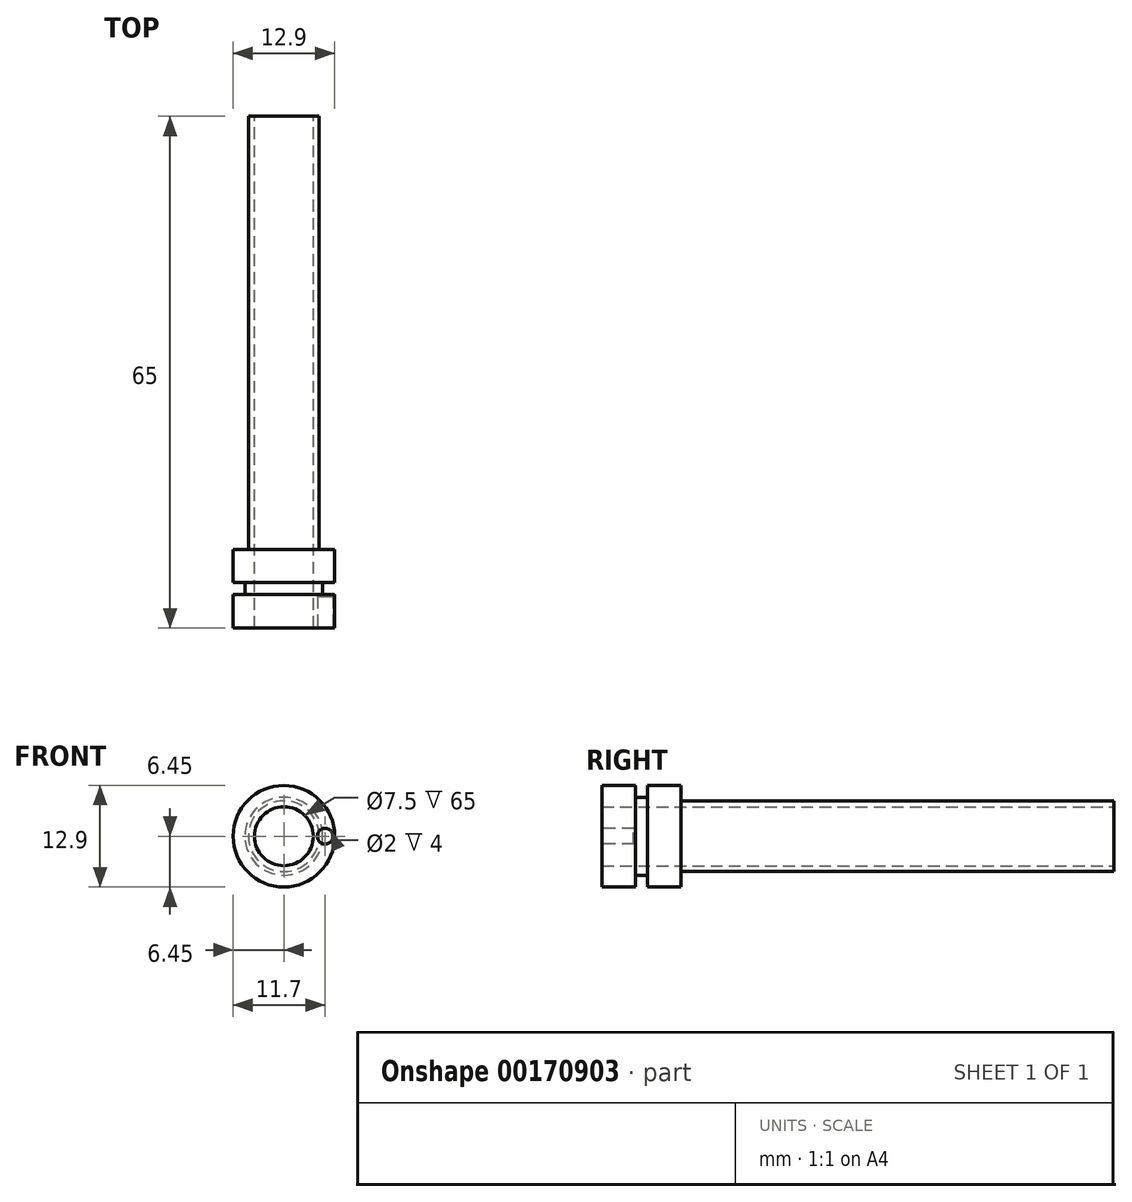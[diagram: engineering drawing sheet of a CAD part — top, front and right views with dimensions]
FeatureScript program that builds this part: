
annotation { "Feature Type Name" : "Feature", "Feature Type Description" : "" }
export const myFeature = defineFeature(function(context is Context, id is Id, definition is map)
    precondition{}
    {
        {
            var Q0;
            Q0=qCreatedBy(makeId("Right.planeOp"),FACE);
            var sketch = newSketch(context, id + "F0", { "sketchPlane" : qUnion([Q0])});
            skLineSegment(sketch, "E0", {"start": v(11.47, 0) * mm, "end": v(0, 0) * mm, "construction": true});
            skLineSegment(sketch, "E1", {"start": v(65, 3.75) * mm, "end": v(0, 3.75) * mm});
            skLineSegment(sketch, "E2", {"start": v(65, 0) * mm, "end": v(65, 3.75) * mm});
            skLineSegment(sketch, "E3", {"start": v(65, 0) * mm, "end": v(65, 0) * mm});
            skLineSegment(sketch, "E4", {"start": v(65, 0) * mm, "end": v(65, 4.5) * mm});
            skLineSegment(sketch, "E5", {"start": v(4.25, 4.95) * mm, "end": v(4.25, 6.45) * mm});
            skLineSegment(sketch, "E6", {"start": v(0, 6.45) * mm, "end": v(4.25, 6.45) * mm});
            skLineSegment(sketch, "E7", {"start": v(0, 6.45) * mm, "end": v(0, 3.75) * mm});
            skLineSegment(sketch, "E8", {"start": v(5.75, 4.95) * mm, "end": v(5.75, 6.45) * mm});
            skLineSegment(sketch, "E9", {"start": v(5.75, 6.45) * mm, "end": v(10, 6.45) * mm});
            skLineSegment(sketch, "E10", {"start": v(10, 6.45) * mm, "end": v(10, 4.5) * mm});
            skLineSegment(sketch, "E11.trimOffspring", {"start": v(5.75, 4.95) * mm, "end": v(4.25, 4.95) * mm});
            skLineSegment(sketch, "E12", {"start": v(10, 4.5) * mm, "end": v(65, 4.5) * mm});
            skSolve(sketch);
        }
        {
            var Q0;
            Q0=makeQuery(id+"F0.imprint","IMPRINT",FACE,{"disambiguationData":[TD([[makeQuery(id+"F0.imprint","IMPRINT",EDGE,{"derivedFrom":sQuery(id+"F0.wireOp",EDGE,"E1")}),-1.0]])]});
            var Q1;
            Q1=sQuery(id+"F0.wireOp",EDGE,"E0");
            revolve(context, id + "F1", {"entities" : qUnion([Q0]), "axis" : qUnion([Q1]), "revolveType" : RevolveType.FULL});
        }
        {
            var Q0;
            Q0=makeQuery(id+"F1.opRevolve","SWEPT_FACE",FACE,{"disambiguationData":[OSD([sQuery(id+"F0.wireOp",EDGE,"E7")])]});
            var sketch = newSketch(context, id + "F2", { "sketchPlane" : qUnion([Q0])});
            skCircle(sketch, "E13", {"center": v(0, 0) * mm, "radius": 5.25 * mm, "construction": true});
            skCircle(sketch, "E14", {"center": v(5.25, 0) * mm, "radius": 1 * mm});
            skSolve(sketch);
        }
        {
            var Q0;
            Q0=makeQuery(id+"F2.imprint","IMPRINT",FACE,{"disambiguationData":[TD([[makeQuery(id+"F2.imprint","IMPRINT",EDGE,{"derivedFrom":sQuery(id+"F2.wireOp",EDGE,"E14")}),1.0]])]});
            extrude(context, id + "F3", {"entities" : qUnion([Q0]), "operationType" : NewBodyOperationType.REMOVE, "oppositeDirection" : true, "depth" : 4 * mm});
        }
    });
